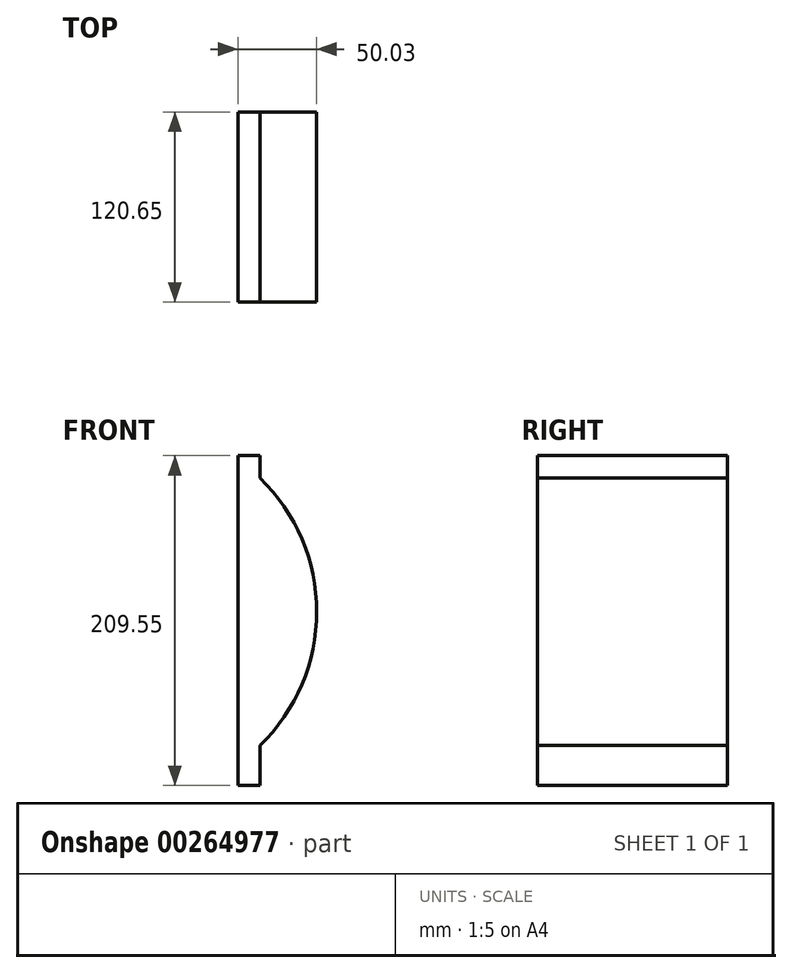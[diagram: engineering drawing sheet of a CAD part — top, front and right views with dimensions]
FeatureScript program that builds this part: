
annotation { "Feature Type Name" : "Feature", "Feature Type Description" : "" }
export const myFeature = defineFeature(function(context is Context, id is Id, definition is map)
    precondition{}
    {
        {
            var Q0;
            Q0=qCreatedBy(makeId("Front.planeOp"),FACE);
            var sketch = newSketch(context, id + "F0", { "sketchPlane" : qUnion([Q0])});
            skLineSegment(sketch, "E0", {"start": v(-35.76, -123.37) * mm, "end": v(-35.76, -97.97) * mm});
            skLineSegment(sketch, "E1", {"start": v(-7.71, 83) * mm, "end": v(-7.46, 83) * mm});
            skLineSegment(sketch, "E2", {"start": v(-7.46, 83) * mm, "end": v(-7.46, 86.18) * mm});
            skLineSegment(sketch, "E3", {"start": v(-35.76, 86.18) * mm, "end": v(-35.76, 71.9) * mm});
            skPoint(sketch, "E4", {"position": v(-4.98, 61.87) * mm});
            skArc(sketch, "E5", {"start": v(-35.76, -97.97) * mm, "mid": v(0.18, -13.03) * mm, "end": v(-35.76, 71.9) * mm});
            skLineSegment(sketch, "E6", {"start": v(-44.5, 62.28) * mm, "end": v(-44.5, 60.87) * mm});
            skPoint(sketch, "E7.visualSharp", {"position": v(-44.5, 60.78) * mm});
            skArc(sketch, "E7.filletArc", {"start": v(-44.5, 60.87) * mm, "mid": v(-44.5, 60.79) * mm, "end": v(-44.46, 60.72) * mm});
            skLineSegment(sketch, "E8", {"start": v(-16.46, 83) * mm, "end": v(-16.2, 83) * mm});
            skLineSegment(sketch, "E9", {"start": v(-16.2, 83) * mm, "end": v(-16.2, 86.18) * mm});
            skPoint(sketch, "E10", {"position": v(-44.25, -13.07) * mm});
            skLineSegment(sketch, "E11", {"start": v(-35.76, 86.18) * mm, "end": v(-44.5, 86.18) * mm});
            skLineSegment(sketch, "E12", {"start": v(-35.76, -123.37) * mm, "end": v(-44.5, -123.37) * mm});
            skLineSegment(sketch, "E13", {"start": v(-44.5, -123.37) * mm, "end": v(-49.85, -123.37) * mm});
            skLineSegment(sketch, "E14", {"start": v(-49.85, -123.37) * mm, "end": v(-49.85, 86.18) * mm});
            skPoint(sketch, "E15.end.orphan", {"position": v(-40.33, 86.18) * mm});
            skLineSegment(sketch, "E16", {"start": v(-44.5, 86.18) * mm, "end": v(-49.85, 86.18) * mm});
            skSolve(sketch);
        }
        {
            var Q0;
            Q0=makeQuery(id+"F0.imprint","IMPRINT",FACE,{"disambiguationData":[TD([[makeQuery(id+"F0.imprint","IMPRINT",EDGE,{"derivedFrom":sQuery(id+"F0.wireOp",EDGE,"E0")}),1.0]])]});
            extrude(context, id + "F1", {"entities" : qUnion([Q0]), "depth" : 120.65 * mm});
        }
    });
